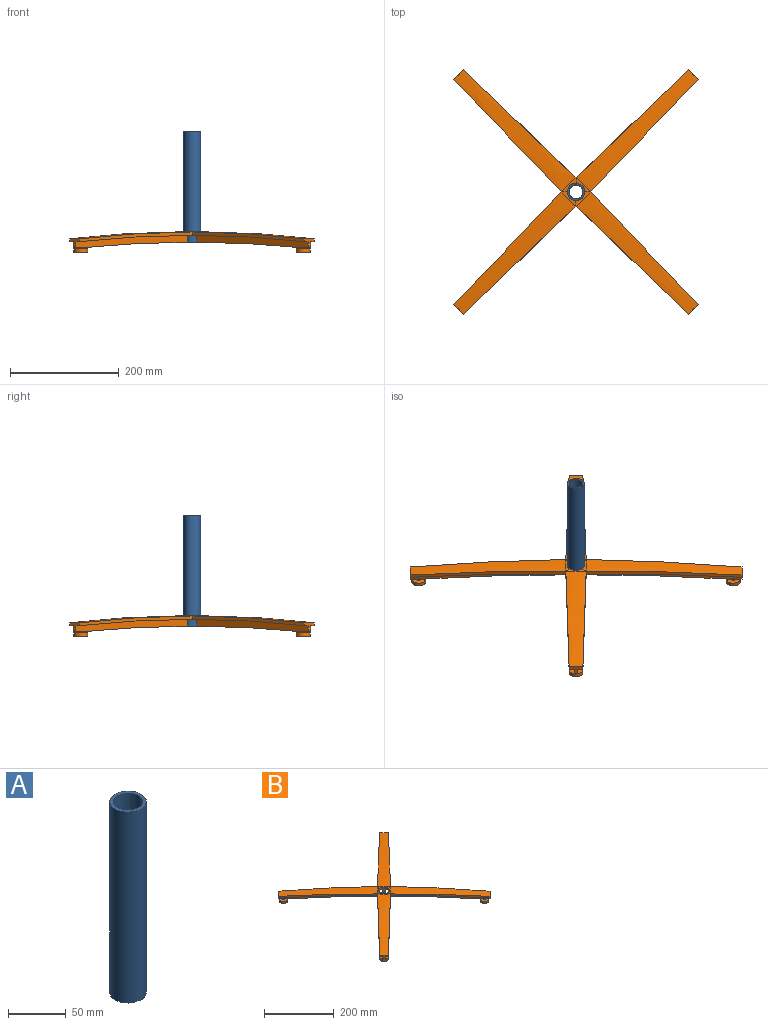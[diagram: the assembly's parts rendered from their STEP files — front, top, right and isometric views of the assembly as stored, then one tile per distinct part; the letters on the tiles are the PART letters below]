
ASSEMBLY  parts=2 mates=1
PART A: 4 faces, bbox 31.8x31.8x203.2 mm
  f0: cylinder r=12.7mm len=203.2mm, axis (0,0,-1), area 16214.6mm2, adj f2,f3
  f1: cylinder r=15.88mm len=203.2mm, axis (0,0,-1), area 20268.3mm2, adj f2,f3
  f2: plane 31.75x31.75mm, normal (0,0,1), area 285mm2, adj f0,f1
  f3: plane 31.75x31.75mm, normal (0,0,-1), area 285mm2, adj f0,f1
PART B: 77 faces, bbox 454x454x42.5 mm
  f0: bspline ~237.98x237.98mm, area 8977.6mm2, adj f1,f8,f9,f73,f75
  f1: bspline ~220.02x211.04mm, area 1623.8mm2, adj f0,f2,f8,f27
  f2: bspline ~226.75x222.26mm, area 3652.3mm2, adj f1,f6,f8,f66,f76
  f3: bspline ~226.75x222.26mm, area 3652.3mm2, adj f7,f8,f9,f64,f76
  f4: plane 11.23x11.23mm, normal (0,0,-1), area 44.6mm2, adj f5,f6,f7,f11
  f5: bspline ~220.02x220.02mm, area 1675.8mm2, adj f4,f6,f7,f76
  f6: plane 205.06x205.06mm, normal (0.71,-0.71,0), area 3662.4mm2, adj f2,f4,f5,f8,f10,f76
  f7: plane 204.55x204.55mm, normal (-0.71,0.71,0), area 3662.4mm2, adj f3,f4,f5,f8,f10,f76
  f8: plane 17.96x17.96mm, normal (0.71,0.71,0), area 197.6mm2, adj f0,f1,f2,f3,f6,f7,f9,f10
  f9: bspline ~220.02x211.04mm, area 1623.8mm2, adj f0,f3,f8,f57
  f10: plane 15.72x15.72mm, normal (0,0,-1), area 85mm2, adj f6,f7,f8,f11
  f11: cylinder r=3.17mm len=6.35mm, axis (0,0,1), area 50.7mm2, adj f4,f10,f14
  f12: plane 25.4x25.4mm, normal (0,0,-1), area 506.7mm2, adj f13
  f13: cylinder r=12.7mm len=25.4mm, axis (0,0,1), area 506.7mm2, adj f12,f14
  f14: plane 25.4x25.4mm, normal (0,0,1), area 475mm2, adj f11,f13
  f15: bspline ~97.36x97.36mm, area 88.7mm2, adj f16,f17,f69,f76
  f16: bspline ~73.42x70.42mm, area 0.8mm2, adj f15,f63,f68
  f17: bspline ~97.36x97.36mm, area 88.7mm2, adj f15,f18,f48,f76
  f18: bspline ~73.42x70.42mm, area 0.8mm2, adj f17,f46,f47
  f19: bspline ~191.06x191.06mm, area 1676.9mm2, adj f42,f43,f44,f76
  f20: bspline ~237.98x237.98mm, area 8977.6mm2, adj f25,f26,f27,f49,f70
  f21: bspline ~226.75x222.26mm, area 3652.3mm2, adj f24,f25,f26,f45,f76
  f22: plane 11.23x11.23mm, normal (0,0,-1), area 44.6mm2, adj f23,f24,f29,f65
  f23: bspline ~191.06x191.06mm, area 1676.9mm2, adj f22,f24,f65,f76
  f24: plane 210.04x210.04mm, normal (-0.71,-0.71,0), area 3662.4mm2, adj f21,f22,f23,f25,f28,f76
  f25: plane 17.96x17.96mm, normal (0.71,-0.71,0), area 197.6mm2, adj f20,f21,f24,f26,f27,f28,f65,f66
  f26: bspline ~220.02x211.04mm, area 1623.8mm2, adj f20,f21,f25,f38
  f27: bspline ~220.02x211.04mm, area 1623.8mm2, adj f1,f20,f25,f66
  f28: plane 15.72x15.72mm, normal (0,0,-1), area 85mm2, adj f24,f25,f29,f65
  f29: cylinder r=3.17mm len=6.35mm, axis (0,0,1), area 50.7mm2, adj f22,f28,f32
  f30: plane 25.4x25.4mm, normal (0,0,-1), area 506.7mm2, adj f31
  f31: cylinder r=12.7mm len=25.4mm, axis (0,0,1), area 506.7mm2, adj f30,f32
  f32: plane 25.4x25.4mm, normal (0,0,1), area 475mm2, adj f29,f31
  f33: plane 25.4x25.4mm, normal (0,0,1), area 475mm2, adj f34,f36
  f34: cylinder r=12.7mm len=25.4mm, axis (0,0,1), area 506.7mm2, adj f33,f35
  f35: plane 25.4x25.4mm, normal (0,0,-1), area 506.7mm2, adj f34
  f36: cylinder r=3.17mm len=6.35mm, axis (0,0,1), area 50.7mm2, adj f33,f37,f44
  f37: plane 15.72x15.72mm, normal (0,0,-1), area 85mm2, adj f36,f41,f42,f43
  f38: bspline ~220.02x211.04mm, area 1623.8mm2, adj f26,f41,f45,f46
  f39: bspline ~226.75x222.26mm, area 3652.3mm2, adj f40,f41,f43,f56,f76
  f40: bspline ~220.02x211.04mm, area 1623.8mm2, adj f39,f41,f46,f62
  f41: plane 17.96x17.96mm, normal (-0.71,-0.71,0), area 197.6mm2, adj f37,f38,f39,f40,f42,f43,f45,f46
  f42: plane 209.53x209.53mm, normal (0.71,-0.71,0), area 3662.4mm2, adj f19,f37,f41,f44,f45,f76
  f43: plane 210.04x210.04mm, normal (-0.71,0.71,0), area 3662.4mm2, adj f19,f37,f39,f41,f44,f76
  f44: plane 11.23x11.23mm, normal (0,0,-1), area 44.6mm2, adj f19,f36,f42,f43
  f45: bspline ~226.75x222.26mm, area 3652.3mm2, adj f21,f38,f41,f42,f76
  f46: bspline ~237.98x237.98mm, area 8977.6mm2, adj f18,f38,f40,f41,f47
  f47: bspline ~73.42x70.42mm, area 0.8mm2, adj f18,f46,f48
  f48: bspline ~97.36x97.36mm, area 88.7mm2, adj f17,f47,f50,f76
  f49: bspline ~73.42x70.42mm, area 0.8mm2, adj f20,f50,f70
  f50: bspline ~97.36x97.36mm, area 88.7mm2, adj f48,f49,f71,f76
  f51: plane 25.4x25.4mm, normal (0,0,1), area 475mm2, adj f52,f54
  f52: cylinder r=12.7mm len=25.4mm, axis (0,0,1), area 506.7mm2, adj f51,f53
  f53: plane 25.4x25.4mm, normal (0,0,-1), area 506.7mm2, adj f52
  f54: cylinder r=3.17mm len=6.35mm, axis (0,0,1), area 50.7mm2, adj f51,f55,f61
  f55: plane 15.72x15.72mm, normal (0,0,-1), area 85mm2, adj f54,f58,f59,f60
  f56: bspline ~226.75x222.26mm, area 3652.3mm2, adj f39,f58,f59,f62,f76
  f57: bspline ~220.02x211.04mm, area 1623.8mm2, adj f9,f58,f63,f64
  f58: plane 17.96x17.96mm, normal (-0.71,0.71,0), area 197.6mm2, adj f55,f56,f57,f59,f60,f62,f63,f64
  f59: plane 209.53x209.53mm, normal (-0.71,-0.71,0), area 3662.4mm2, adj f55,f56,f58,f61,f67,f76
  f60: plane 210.04x210.04mm, normal (0.71,0.71,0), area 3662.4mm2, adj f55,f58,f61,f64,f67,f76
  f61: plane 11.23x11.23mm, normal (0,0,-1), area 44.6mm2, adj f54,f59,f60,f67
  f62: bspline ~220.02x211.04mm, area 1623.8mm2, adj f40,f56,f58,f63
  f63: bspline ~237.98x237.98mm, area 8977.6mm2, adj f16,f57,f58,f62,f68
  f64: bspline ~226.75x222.26mm, area 3652.3mm2, adj f3,f57,f58,f60,f76
  f65: plane 209.53x209.53mm, normal (0.71,0.71,0), area 3662.4mm2, adj f22,f23,f25,f28,f66,f76
  f66: bspline ~226.75x222.26mm, area 3652.3mm2, adj f2,f25,f27,f65,f76
  f67: bspline ~191.06x191.06mm, area 1676.9mm2, adj f59,f60,f61,f76
  f68: bspline ~73.42x70.42mm, area 0.8mm2, adj f16,f63,f69
  f69: bspline ~97.36x97.36mm, area 88.7mm2, adj f15,f68,f74,f76
  f70: bspline ~73.42x70.42mm, area 0.8mm2, adj f20,f49,f71
  f71: bspline ~97.36x97.36mm, area 88.7mm2, adj f50,f70,f72,f76
  f72: bspline ~97.36x97.36mm, area 88.7mm2, adj f71,f73,f74,f76
  f73: bspline ~73.42x70.42mm, area 0.8mm2, adj f0,f72,f75
  f74: bspline ~97.36x97.36mm, area 88.7mm2, adj f69,f72,f75,f76
  f75: bspline ~73.42x70.42mm, area 0.8mm2, adj f0,f73,f74
  f76: cylinder r=15.88mm len=31.75mm, axis (0,0,1), area 955.7mm2, adj f2,f3,f5,f6,f7,f15,f17,f19
PLACE A at identity
PLACE B rot(axis=(0,0,1),90deg) t=(0,0,19.17)mm
MATE fastened A.f1 <-> B.f76  axis (0,0,-1) through (0,0,0)mm
